# Revit family: Hager-Type B SP&N Distribution Boards-Surface_mounted-IP3X-With_Cover-Without_DIN-Hosted-GB-en
name_source: partatom
category: Electrical Equipment
units: mm (PartAtom-declared; Revit-internal decimal feet)

## family parameters
Cut with Voids When Loaded = No
Host = Face
Maintain Annotation Orientation = Yes
Panel Configuration = Two Columns, Circuits Across
Part Type = Panelboard
Room Calculation Point = No
Round Connector Dimension = Use Diameter
Shared = No

## types (19) — shared parameters
BC_MODEL_ID = 1554199
BC_OBJECT_ID = 513821
BC_OBJECT_VERSION = #1
Code hager = ADD-EC000214_EU
EF000003 - Mounting method = Surface mounted
EF000024 - UV resistant = No
EF000116 - RAL number = 7035
EF000118 - With mounting plate = No
EF001062 - EMC-version = No
EF001134 - With DIN-rail = No
EF005474 - Degree of protection (IP rating) = IP3X
EF015776 - Earthing terminal block = No
EF015777 - Neutral terminal block = No
EF015941 - Signal passing door = No
ETIM class code = EC000214
ETIM class name = Small distribution board
HG000002-With door or cover = Yes
HG000003-Range = Type B SP&N Distribution Boards
HG000005-Thickness = 2 mm  [stored 0.00656168 ft]
HG000006-Flush mounted = No
HG000009-Double swing door = No
HG000010-Asymmetric doors = No
HG000011-Empty rows from bottom = No
HG000012-Door swing angle = 90.00°
HG000013-Door on the left = No
HG000014-Door on the right = Yes
HG000015-Clearance visibility = Yes
HG000016-Door 3D visibility = Yes
HG000017-Distance between poles = 18 mm  [stored 0.0590551 ft]
HG000060-RAL-number = 7035
HG000099-Onfly Template ID = 507532
Manufacturer = Hager
Name = Type B SP&N Distribution Boards-Surface_mounted-IP3X-With_Cover-Without_DIN-GB
Name BIM&CO = Electricity
Name hager = ADD_Enclosures_EC000214
Uniformat = Low Tension Service & Dist.
Uniformat code = D501001
zero-valued in all types: Default Elevation, EF000218 - Recess depth, EF000266 - Number of rows, EF000332 - Recess height, EF000846 - Recess width, EF001131 - Internal depth, EF002950 - Width in number of modular spacings, HG000007-Number of empty columns, HG000008-Number of empty rows, HGEF000266-Number of rows, HGEF002950-Width in number of modular spacings

## per-type parameters (varying)
| type | BC_VARIANT_ID | EF000007 - Colour | EF000008 - Width | EF000040 - Height | EF000049 - Depth | EF001088 - Extension possible | EF006244 - Transparent cover/door | EF006306 - With lock | HG000001-Number of columns | HG000004-Manufacturer reference |
| Type B SP&N Distribution Boards-Surface_mounted_W465_H305_D55_0_Modular_Spacing-JK101DK | 1178573 |  | 465 mm  [stored 1.52559 ft] | 305 mm  [stored 1.00066 ft] | 55 mm  [stored 0.180446 ft] | No | No | No | 1 | JK101DK |
| Type B SP&N Distribution Boards-Surface_mounted_W465_H450_D55_0_Modular_Spacing-JK102DK | 1178574 |  | 465 mm  [stored 1.52559 ft] | 450 mm  [stored 1.47638 ft] | 55 mm  [stored 0.180446 ft] | No | No | No | 1 | JK102DK |
| Type B SP&N Distribution Boards-Surface_mounted_W465_H500_D91_0_Modular_Spacing-JK104BSF | 1178575 | Grey | 465 mm  [stored 1.52559 ft] | 500 mm  [stored 1.64042 ft] | 91 mm  [stored 0.298556 ft] | Yes | Yes | No | 0 | JK104BSF |
| Type B SP&N Distribution Boards-Surface_mounted_W465_H500_D91_0_Modular_Spacing-JK104BSH | 1178576 | Grey | 465 mm  [stored 1.52559 ft] | 500 mm  [stored 1.64042 ft] | 91 mm  [stored 0.298556 ft] | Yes | Yes | Yes | 0 | JK104BSH |
| Type B SP&N Distribution Boards-Surface_mounted_W465_H550_D91_0_Modular_Spacing-JK106BSF | 1178577 | Grey | 465 mm  [stored 1.52559 ft] | 550 mm | 91 mm  [stored 0.298556 ft] | Yes | Yes | No | 0 | JK106BSF |
| Type B SP&N Distribution Boards-Surface_mounted_W465_H625_D91_0_Modular_Spacing-JK108BSF | 1178578 | Grey | 465 mm  [stored 1.52559 ft] | 625 mm  [stored 2.05052 ft] | 91 mm  [stored 0.298556 ft] | Yes | No | No | 0 | JK108BSF |
| Type B SP&N Distribution Boards-Surface_mounted_W465_H850_D91_0_Modular_Spacing-JK112BSF | 1178579 | Grey | 465 mm  [stored 1.52559 ft] | 850 mm  [stored 2.78871 ft] | 91 mm  [stored 0.298556 ft] | Yes | No | No | 0 | JK112BSF |
| Type B SP&N Distribution Boards-Surface_mounted_W465_H950_D91_0_Modular_Spacing-JK116BSF | 1178580 | Grey | 465 mm  [stored 1.52559 ft] | 950 mm  [stored 3.1168 ft] | 91 mm  [stored 0.298556 ft] | Yes | No | No | 0 | JK116BSF |
| Type B SP&N Distribution Boards-Surface_mounted_W465_H950_D91_0_Modular_Spacing-JK116BSH | 1178581 | Grey | 465 mm  [stored 1.52559 ft] | 950 mm  [stored 3.1168 ft] | 91 mm  [stored 0.298556 ft] | Yes | No | No | 0 | JK116BSH |
| Type B SP&N Distribution Boards-Surface_mounted_W465_H950_D124_0_Modular_Spacing-JK208BSF | 1178582 | Grey | 465 mm  [stored 1.52559 ft] | 950 mm  [stored 3.1168 ft] | 124 mm  [stored 0.406824 ft] | Yes | No | No | 0 | JK208BSF |
| Type B SP&N Distribution Boards-Surface_mounted_W232_H950_D124_0_Modular_Spacing-JK208BSH | 1178583 | Grey | 232 mm  [stored 0.761155 ft] | 950 mm  [stored 3.1168 ft] | 124 mm  [stored 0.406824 ft] | Yes | No | No | 0 | JK208BSH |
| Type B SP&N Distribution Boards-Surface_mounted_W465_H1100_D166_0_Modular_Spacing-JK212BSF | 1178584 | Grey | 465 mm  [stored 1.52559 ft] | 1100 mm | 166 mm  [stored 0.544619 ft] | Yes | No | No | 0 | JK212BSF |
| Type B SP&N Distribution Boards-Surface_mounted_W232_H1100_D166_0_Modular_Spacing-JK212BSH | 1178585 | Grey | 232 mm  [stored 0.761155 ft] | 1100 mm | 166 mm  [stored 0.544619 ft] | Yes | No | No | 0 | JK212BSH |
| Type B SP&N Distribution Boards-Surface_mounted_W465_H1250_D166_0_Modular_Spacing-JK216BSF | 1178586 | Grey | 465 mm  [stored 1.52559 ft] | 1250 mm  [stored 4.10105 ft] | 166 mm  [stored 0.544619 ft] | Yes | No | No | 0 | JK216BSF |
| Type B SP&N Distribution Boards-Surface_mounted_W232_H1250_D166_0_Modular_Spacing-JK216BSH | 1178587 | Grey | 232 mm  [stored 0.761155 ft] | 1250 mm  [stored 4.10105 ft] | 166 mm  [stored 0.544619 ft] | Yes | No | No | 0 | JK216BSH |
| Type B SP&N Distribution Boards-Surface_mounted_W465_H1400_D166_0_Modular_Spacing-JK218BSF | 1178588 | Grey | 465 mm  [stored 1.52559 ft] | 1400 mm  [stored 4.59318 ft] | 166 mm  [stored 0.544619 ft] | Yes | No | No | 0 | JK218BSF |
| Type B SP&N Distribution Boards-Surface_mounted_W232_H1400_D166_0_Modular_Spacing-JK218BSH | 1178589 | Grey | 232 mm  [stored 0.761155 ft] | 1400 mm  [stored 4.59318 ft] | 166 mm  [stored 0.544619 ft] | Yes | No | No | 0 | JK218BSH |
| Type B SP&N Distribution Boards-Surface_mounted_W465_H1550_D124_0_Modular_Spacing-JK224BSF | 1178590 | Grey | 465 mm  [stored 1.52559 ft] | 1550 mm  [stored 5.0853 ft] | 124 mm  [stored 0.406824 ft] | Yes | No | No | 0 | JK224BSF |
| Type B SP&N Distribution Boards-Surface_mounted_W232_H1550_D124_0_Modular_Spacing-JK224BSH | 1178591 | Grey | 232 mm  [stored 0.761155 ft] | 1550 mm  [stored 5.0853 ft] | 124 mm  [stored 0.406824 ft] | Yes | No | No | 0 | JK224BSH |

note: column(s) folded — value = type name in every type: Reference

note: [stored X ft] marks values corroborated as IEEE doubles in the binary element streams (Revit-internal decimal feet)

## geometry (parser evidence)
native form markers: Sweep x13
no freeform markers — native parametric forms only
